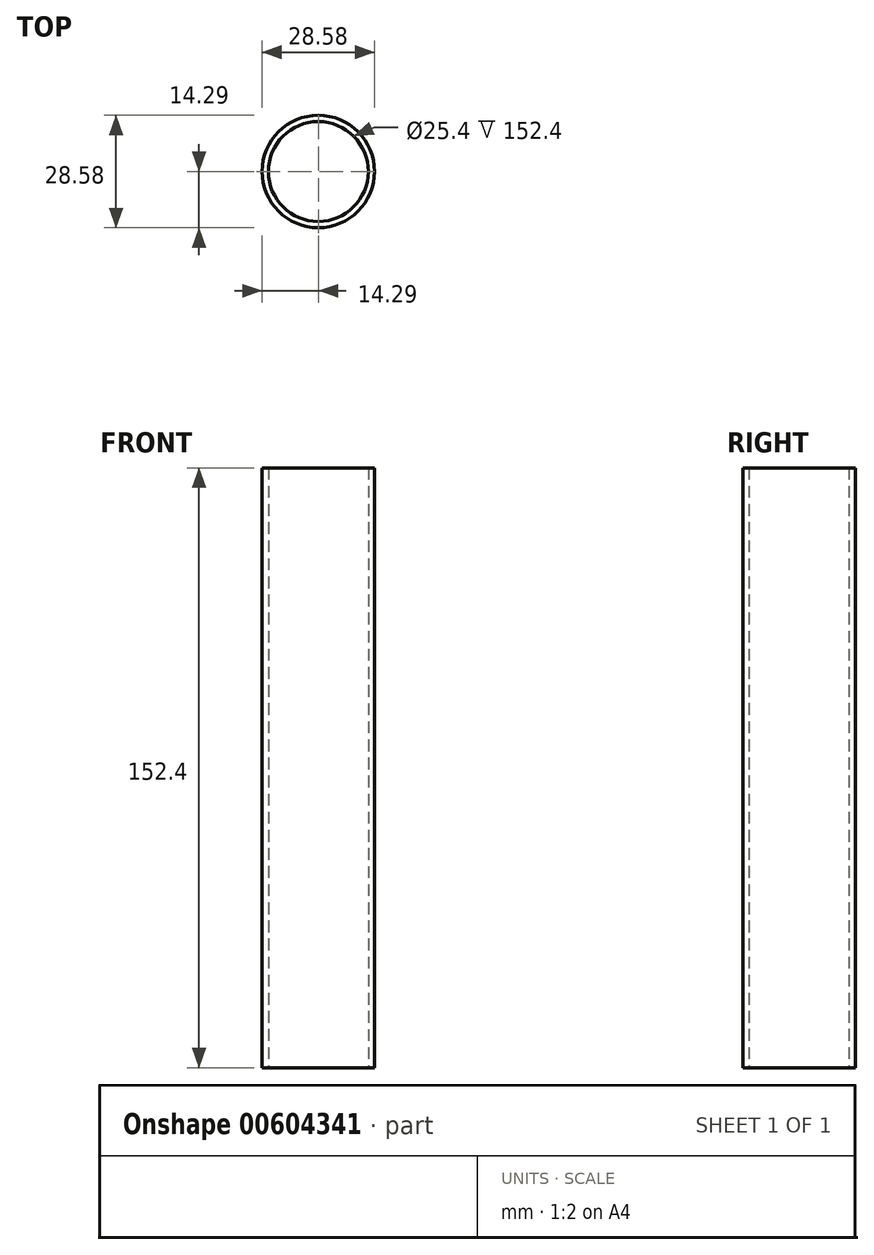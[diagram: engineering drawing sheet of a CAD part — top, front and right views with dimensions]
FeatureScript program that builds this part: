
annotation { "Feature Type Name" : "Feature", "Feature Type Description" : "" }
export const myFeature = defineFeature(function(context is Context, id is Id, definition is map)
    precondition{}
    {
        {
            var Q0;
            Q0=qCreatedBy(makeId("Top.planeOp"),FACE);
            var sketch = newSketch(context, id + "F0", { "sketchPlane" : qUnion([Q0])});
            skLineSegment(sketch, "E0", {"start": v(0, 0) * mm, "end": v(12.7, 0) * mm});
            skCircle(sketch, "E1", {"center": v(0, 0) * mm, "radius": 12.7 * mm});
            skCircle(sketch, "E2.0", {"center": v(0, 0) * mm, "radius": 14.29 * mm});
            skSolve(sketch);
        }
        {
            var Q0;
            Q0=qCreatedBy(makeId("Top.planeOp"),FACE);
            var sketch = newSketch(context, id + "F1", { "sketchPlane" : qUnion([Q0])});
            skSolve(sketch);
        }
        {
            var Q0;
            Q0 = qSketchRegion(id + "F1", true);
            var Q1;
            Q1=makeQuery(id+"F0.imprint","IMPRINT",FACE,{"disambiguationData":[TD([[makeQuery(id+"F0.imprint","IMPRINT",EDGE,{"derivedFrom":sQuery(id+"F0.wireOp",EDGE,"E1")}),-1.0]])]});
            extrude(context, id + "F2", {"entities" : qUnion([Q0, Q1]), "depth" : 152.4 * mm, "offsetDistance" : 25.4 * mm});
        }
    });
